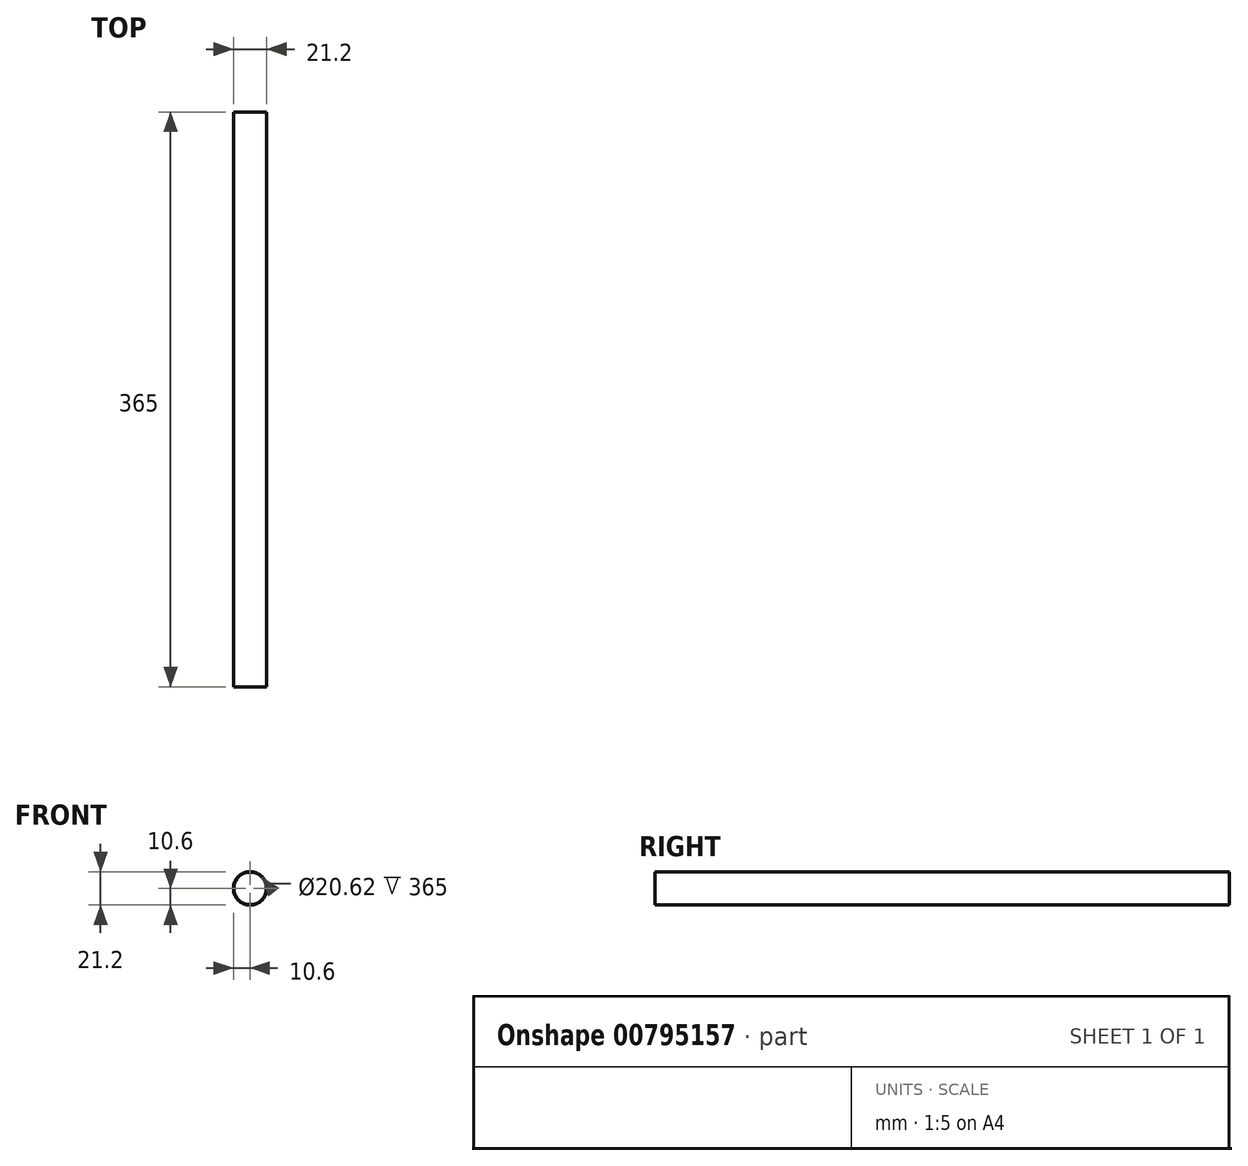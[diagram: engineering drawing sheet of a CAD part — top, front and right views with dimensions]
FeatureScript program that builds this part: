
annotation { "Feature Type Name" : "Feature", "Feature Type Description" : "" }
export const myFeature = defineFeature(function(context is Context, id is Id, definition is map)
    precondition{}
    {
        {
            var Q0;
            Q0=qCreatedBy(makeId("Front.planeOp"),FACE);
            var sketch = newSketch(context, id + "F0", { "sketchPlane" : qUnion([Q0])});
            skCircle(sketch, "E0", {"center": v(0, 0) * mm, "radius": 10.6 * mm});
            skCircle(sketch, "E1", {"center": v(0, 0) * mm, "radius": 10.31 * mm});
            skSolve(sketch);
        }
        {
            var Q0;
            Q0=makeQuery(id+"F0.imprint","IMPRINT",FACE,{"disambiguationData":[TD([[makeQuery(id+"F0.imprint","IMPRINT",EDGE,{"derivedFrom":sQuery(id+"F0.wireOp",EDGE,"E0")}),1.0]])]});
            extrude(context, id + "F1", {"entities" : qUnion([Q0]), "depth" : 365 * mm, "offsetDistance" : 25 * mm});
        }
    });
